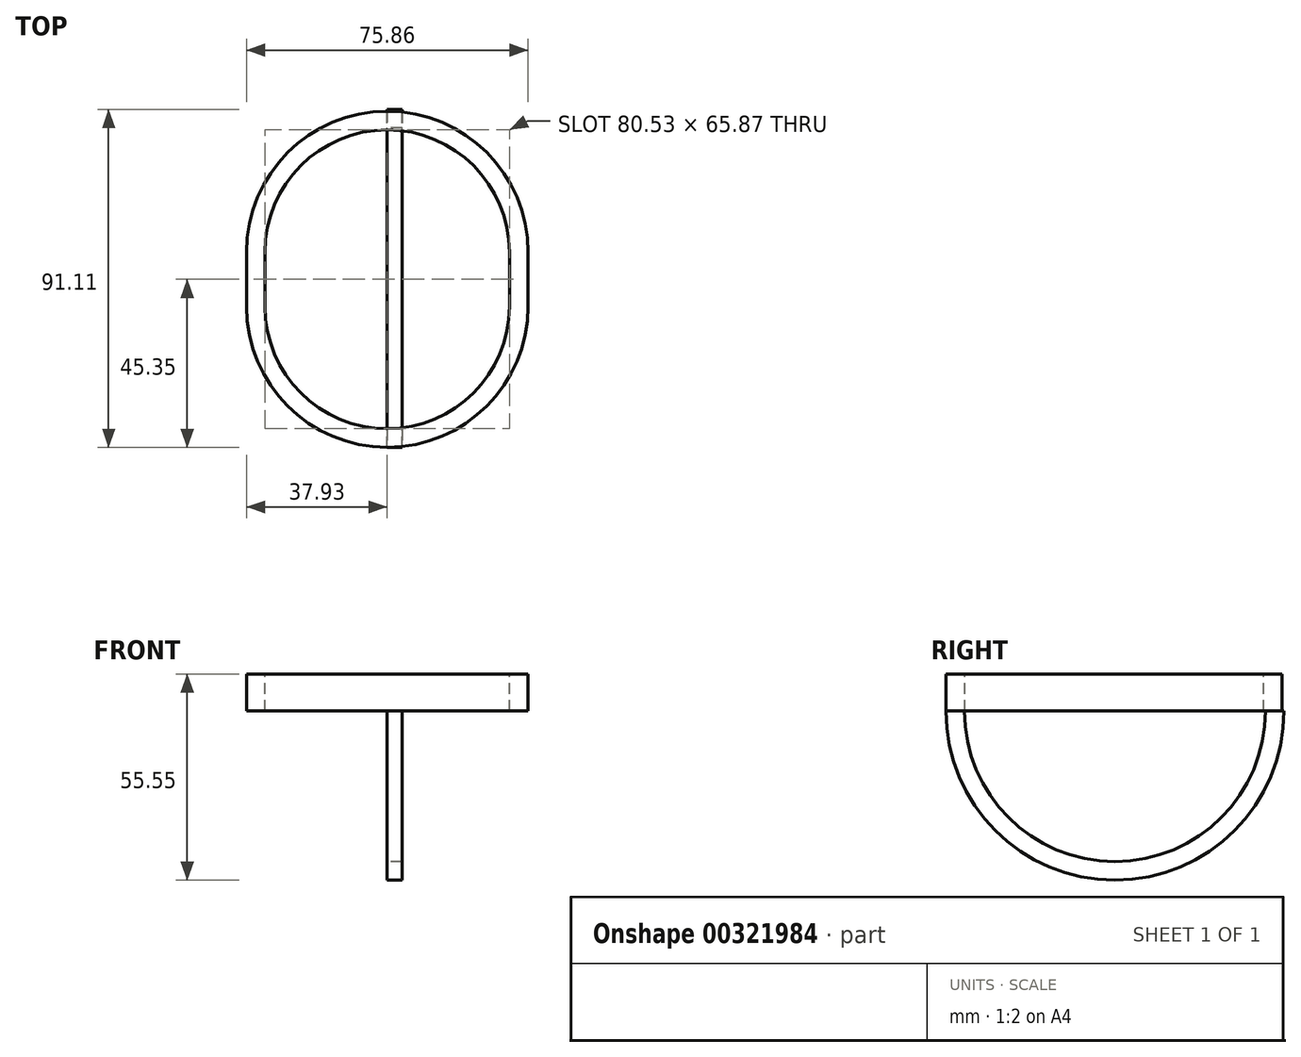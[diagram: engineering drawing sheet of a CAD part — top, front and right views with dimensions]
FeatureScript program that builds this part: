
annotation { "Feature Type Name" : "Feature", "Feature Type Description" : "" }
export const myFeature = defineFeature(function(context is Context, id is Id, definition is map)
    precondition{}
    {
        {
            var Q0;
            Q0=qCreatedBy(makeId("Top.planeOp"),FACE);
            var sketch = newSketch(context, id + "F0", { "sketchPlane" : qUnion([Q0])});
            skArc(sketch, "E0", {"start": v(37.93, 0) * mm, "mid": v(0, 37.93) * mm, "end": v(-37.93, 0) * mm});
            skLineSegment(sketch, "E1", {"start": v(-37.93, 0) * mm, "end": v(-37.93, -14.66) * mm});
            skLineSegment(sketch, "E2", {"start": v(37.93, 0) * mm, "end": v(37.93, -14.66) * mm});
            skArc(sketch, "E3", {"start": v(37.93, -14.66) * mm, "mid": v(0, -52.6) * mm, "end": v(-37.93, -14.66) * mm});
            skArc(sketch, "E4.0", {"start": v(32.93, -14.66) * mm, "mid": v(0, -47.6) * mm, "end": v(-32.93, -14.66) * mm});
            skLineSegment(sketch, "E4.1", {"start": v(32.93, 0) * mm, "end": v(32.93, -14.66) * mm});
            skArc(sketch, "E4.2", {"start": v(32.93, 0) * mm, "mid": v(0, 32.93) * mm, "end": v(-32.93, 0) * mm});
            skLineSegment(sketch, "E4.3", {"start": v(-32.93, 0) * mm, "end": v(-32.93, -14.66) * mm});
            skSolve(sketch);
        }
        {
            var Q0;
            Q0 = qSketchRegion(id + "F0", true);
            extrude(context, id + "F1", {"entities" : qUnion([Q0]), "oppositeDirection" : true, "depth" : 10 * mm});
        }
        {
            var Q0;
            Q0=qCreatedBy(makeId("Right.planeOp"),FACE);
            var sketch = newSketch(context, id + "F2", { "sketchPlane" : qUnion([Q0])});
            skPoint(sketch, "E5", {"position": v(38.43, 0) * mm});
            skPoint(sketch, "E6", {"position": v(38.43, -10) * mm});
            skLineSegment(sketch, "E7", {"start": v(38.43, -10) * mm, "end": v(38.43, 0) * mm});
            skPoint(sketch, "E8", {"position": v(-52.68, 0) * mm});
            skPoint(sketch, "E9", {"position": v(-52.68, -10) * mm});
            skLineSegment(sketch, "E10", {"start": v(-52.68, 0) * mm, "end": v(-52.68, -10) * mm});
            skArc(sketch, "E11", {"start": v(-52.68, -10) * mm, "mid": v(-7.12, -55.55) * mm, "end": v(38.43, -10) * mm});
            skArc(sketch, "E12.0", {"start": v(-47.68, -10) * mm, "mid": v(-5.48, -50.52) * mm, "end": v(33.3, -6.72) * mm});
            skLineSegment(sketch, "E13", {"start": v(-47.68, -10) * mm, "end": v(-52.68, -10) * mm});
            skLineSegment(sketch, "E14", {"start": v(38.43, -10) * mm, "end": v(33.43, -10) * mm});
            skSolve(sketch);
        }
        {
            var Q0;
            Q0 = qSketchRegion(id + "F2", true);
            extrude(context, id + "F3", {"entities" : qUnion([Q0]), "operationType" : NewBodyOperationType.ADD, "depth" : 4 * mm});
        }
        {
            var Q0;
            Q0=qCreatedBy(makeId("Front.planeOp"),FACE);
            cPlane(context, id + "F4", {"entities" : qUnion([Q0]), "cplaneType" : CPlaneType.OFFSET, "offset" : 7.5 * mm, "width" : 150 * mm, "height" : 150 * mm});
        }
    });
